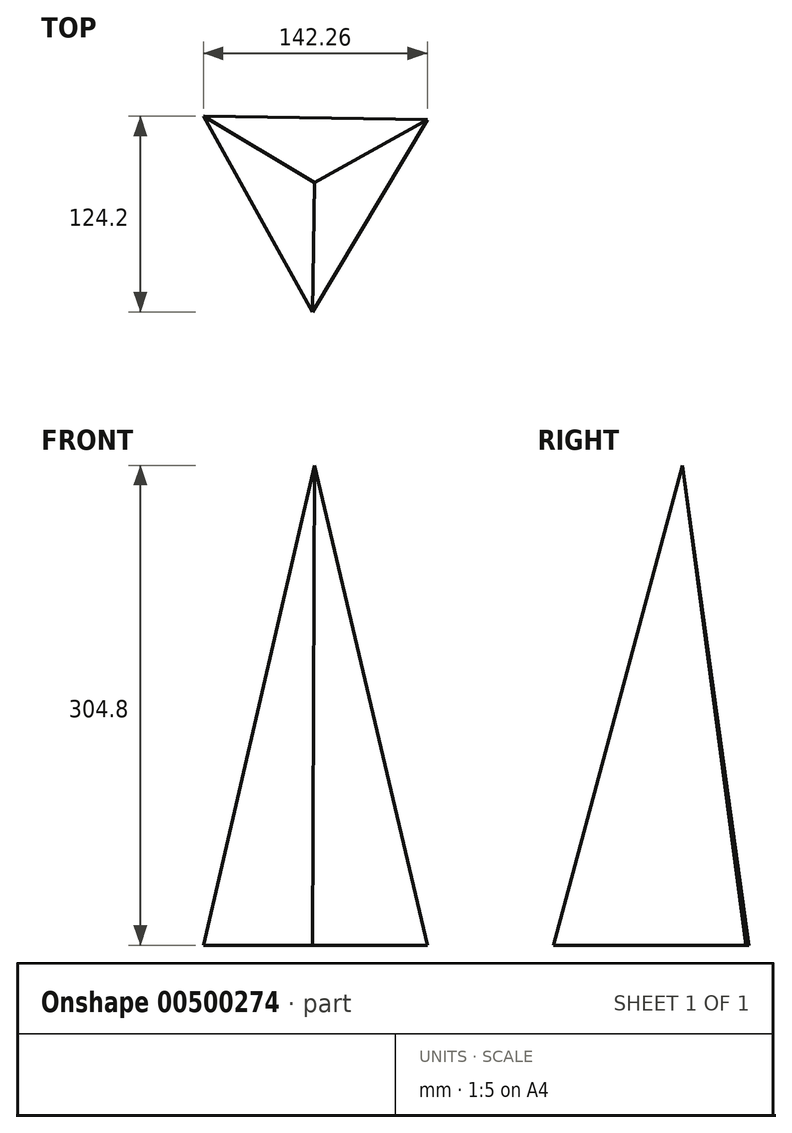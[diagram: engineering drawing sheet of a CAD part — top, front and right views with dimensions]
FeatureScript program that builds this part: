
annotation { "Feature Type Name" : "Feature", "Feature Type Description" : "" }
export const myFeature = defineFeature(function(context is Context, id is Id, definition is map)
    precondition{}
    {
        {
            var Q0;
            Q0=qCreatedBy(makeId("Top.planeOp"),FACE);
            var sketch = newSketch(context, id + "F0", { "sketchPlane" : qUnion([Q0])});
            skCircle(sketch, "E0.cCircle", {"center": v(0, 0) * mm, "radius": 82.14 * mm, "construction": true});
            skLineSegment(sketch, "E0.0", {"start": v(71.7, 40.08) * mm, "end": v(-1.14, -82.14) * mm});
            skLineSegment(sketch, "E0.1", {"start": v(-1.14, -82.14) * mm, "end": v(-70.56, 42.06) * mm});
            skLineSegment(sketch, "E0.2", {"start": v(-70.56, 42.06) * mm, "end": v(71.7, 40.08) * mm});
            skSolve(sketch);
        }
        {
            var Q0;
            Q0=qCreatedBy(makeId("Top.planeOp"),FACE);
            cPlane(context, id + "F1", {"entities" : qUnion([Q0]), "cplaneType" : CPlaneType.OFFSET, "offset" : 304.8 * mm, "width" : 152.4 * mm, "height" : 152.4 * mm});
        }
        {
            var Q0;
            Q0=qCreatedBy(id+"F1.planeOp",FACE);
            var sketch = newSketch(context, id + "F2", { "sketchPlane" : qUnion([Q0])});
            skPoint(sketch, "E1", {"position": v(0, 0) * mm});
            skSolve(sketch);
        }
        {
            var Q0;
            Q0=sQuery(id+"F2.wireOp",VERTEX,"E1");
            var Q1;
            Q1=makeQuery(id+"F0.imprint","IMPRINT",FACE,{"disambiguationData":[TD([[makeQuery(id+"F0.imprint","IMPRINT",EDGE,{"derivedFrom":sQuery(id+"F0.wireOp",EDGE,"E0.0")}),-1.0]])]});
            loft(context, id + "F3", {"sheetProfilesArray" : [{ "sheetProfileEntities" : qUnion([Q0]) }, { "sheetProfileEntities" : qUnion([Q1]) }]});
        }
    });
